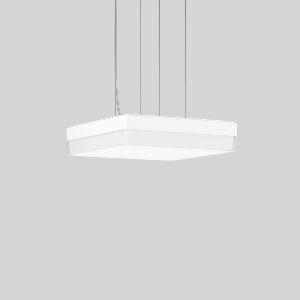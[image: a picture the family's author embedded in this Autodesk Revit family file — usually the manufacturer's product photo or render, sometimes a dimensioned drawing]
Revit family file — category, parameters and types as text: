
# Revit family: flat_slim_square_312542_002_5d0e
name_source: partatom
category: Lighting Fixtures
units: mm (PartAtom-declared; Revit-internal decimal feet)

## family parameters
Cut with Voids When Loaded = No
Host = Face
Light Source = No
Part Type = Normal
Room Calculation Point = No
Round Connector Dimension = Use Diameter
Shared = No

## types (1)
- MultiLumen 2 840 (1 x LED Modul 840, 2200 lm, 4000)
    Apparent Load = 19 VA
    CIE Flux Codes = 43 75 93 91 100
    Color Rendering = 80
    Color Temperature = 4000
    Default Elevation = 1800 mm
    Height = 70 mm
    Lamp = 1 x LED Modul 840
    Lamp Light Flux = 2200 lm
    Lamp count = 1
    Length = 300 mm
    Lifetime = 50000 h
    Luminous efficacy = 116 lm/W
    Manufacturer = RZB
    ModVariant = No
    Model = 312542.002
    Mounting Place = Ceiling
    Mounting Type = Pendant
    Number of Poles = 1
    OnlyDefault = Yes
    Power Factor = 1
    Product Name = FLAT SLIM square
    Product group = Pendant luminaires
    ProductGroupID = 902
    Protection Class = Protection class I
    Protection Degree = IP 40
    RLX_Detail_Level = 1
    RLX_Emergency_Light_Flux = 0 lm
    RLX_Emergency_Type = 0
    RLX_Emergency_Type_DB = No
    RlxData = <blob elided: 13657 chars, md5=38b9025c>
    Socket = socket
    Standby Power = 0 W
    System Light Flux = 2200 lm
    System Power = 19 W
    Type Comments = MultiLumen 2 840
    Type Image = 312542.002.jpg
    URL = http://relux.com
    VarID = multilumen_2_840
    Voltage = 230 V
    Voltage Range = 220-240 V
    Weight = 0.00 kg
    Width = 300 mm

## geometry (parser evidence)
native form markers: Sweep x12
no freeform markers — native parametric forms only
